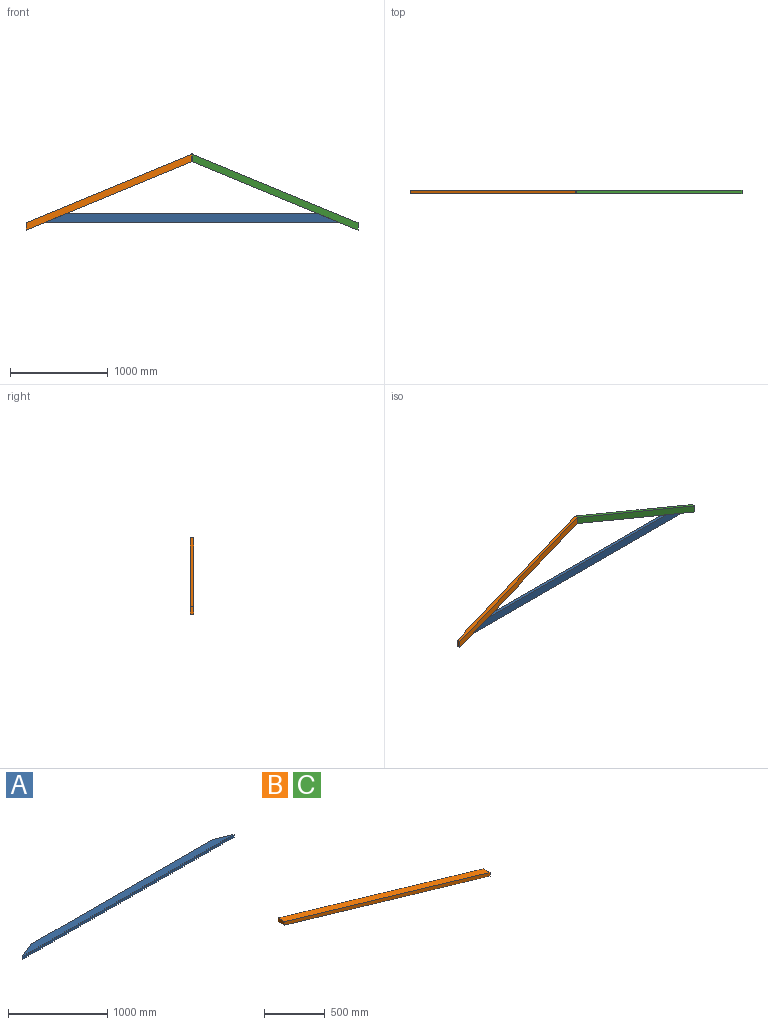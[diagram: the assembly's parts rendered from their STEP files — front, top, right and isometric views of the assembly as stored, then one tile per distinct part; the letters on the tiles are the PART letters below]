
ASSEMBLY  parts=3 mates=2
PART A: 6 faces, bbox 3025x90x35 mm
  f0: plane 217.28x90mm, normal (-0.38,0.92,0), area 8231.3mm2, adj f1,f3,f4,f5
  f1: plane 3025x35mm, normal (0,-1,0), area 105875mm2, adj f0,f2,f4,f5
  f2: plane 217.28x90mm, normal (0.38,0.92,0), area 8231.3mm2, adj f1,f3,f4,f5
  f3: plane 2590.44x35mm, normal (0,1,0), area 90665.5mm2, adj f0,f2,f4,f5
  f4: plane 3025x90mm, normal (0,0,1), area 252694.9mm2, adj f0,f1,f2,f3
  f5: plane 3025x90mm, normal (0,0,-1), area 252694.9mm2, adj f0,f1,f2,f3
PART B: 6 faces, bbox 1697.3x778.8x35 mm
  f0: plane 1697.28x703.03mm, normal (0.38,0.92,0), area 64299.1mm2, adj f2,f3,f4,f5
  f1: plane 1697.28x703.03mm, normal (-0.38,-0.92,0), area 64299.1mm2, adj f2,f3,f4,f5
  f2: plane 1697.28x778.8mm, normal (0,0,1), area 128598.3mm2, adj f0,f1,f4,f5
  f3: plane 1697.28x778.8mm, normal (0,0,-1), area 128598.3mm2, adj f0,f1,f4,f5
  f4: plane 75.77x35mm, normal (-1,0,0), area 2651.9mm2, adj f0,f1,f2,f3
  f5: plane 75.77x35mm, normal (1,0,0), area 2651.9mm2, adj f0,f1,f2,f3
PART C: same geometry as B
PLACE A rot(axis=(1,0,0),90deg) t=(-21.29,83.66,1359.21)mm
PLACE B rot(axis=(0,0.71,0.71),180deg) t=(1249.86,48.66,1580.04)mm
PLACE C rot(axis=(1,0,0),90deg) t=(-1247.87,83.66,1580.04)mm
MATE fastened A.f2 <-> C.f1  axis (0.38,0,0.92) through (1513.49,66.16,-610.11)mm
MATE fastened B.f4 <-> C.f4  axis (1,0,0) through (0.99,66.16,54.27)mm
